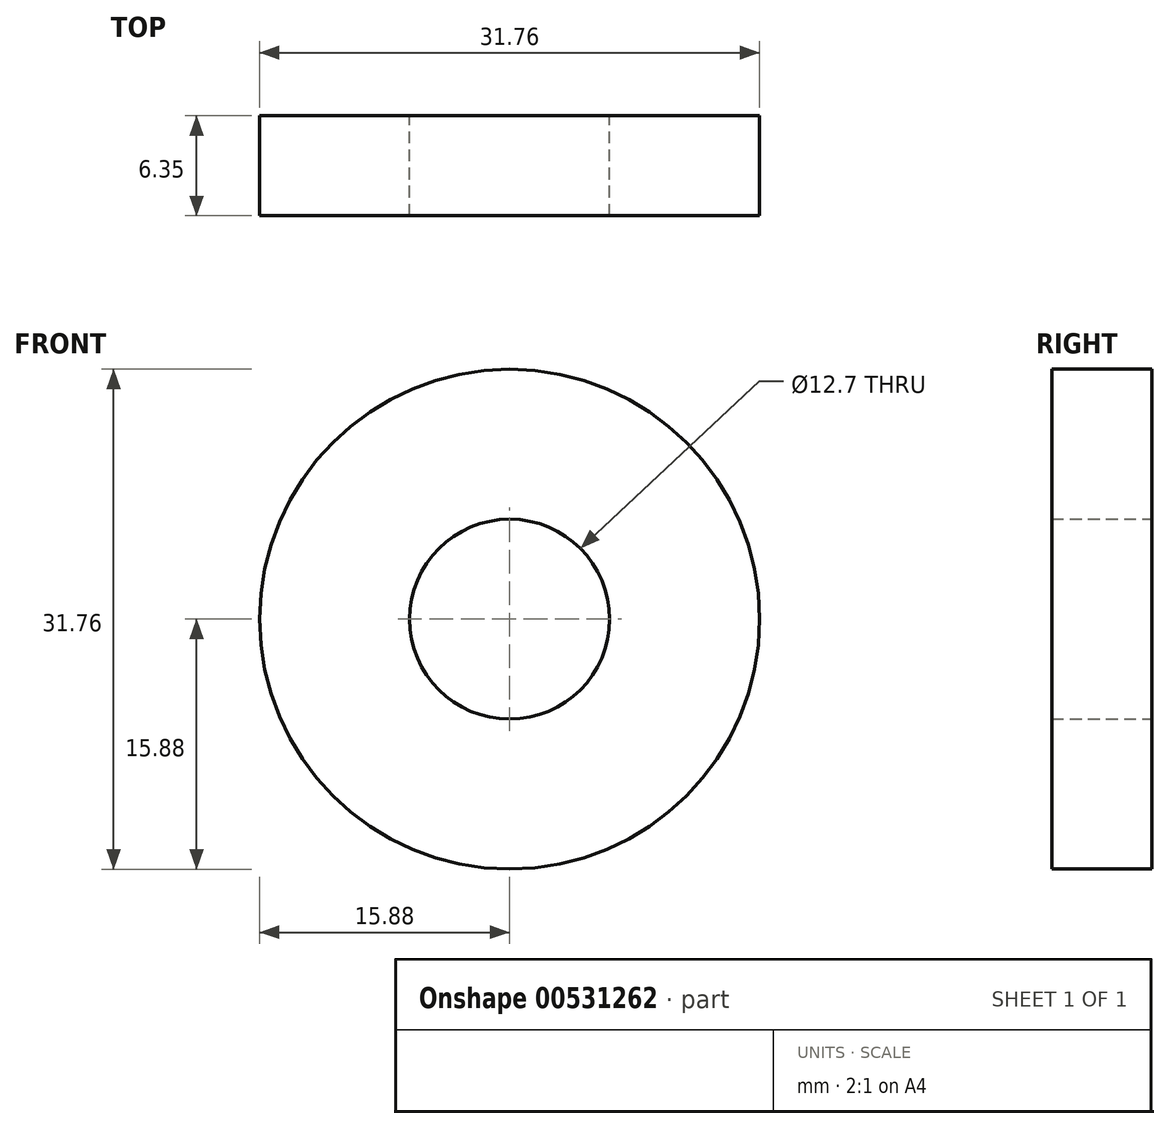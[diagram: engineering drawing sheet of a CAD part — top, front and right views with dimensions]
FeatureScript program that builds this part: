
annotation { "Feature Type Name" : "Feature", "Feature Type Description" : "" }
export const myFeature = defineFeature(function(context is Context, id is Id, definition is map)
    precondition{}
    {
        {
            var Q0;
            Q0=qCreatedBy(makeId("Front.planeOp"),FACE);
            var sketch = newSketch(context, id + "F0", { "sketchPlane" : qUnion([Q0])});
            skCircle(sketch, "E0", {"center": v(0, 0) * mm, "radius": 15.88 * mm});
            skCircle(sketch, "E1", {"center": v(0, 0) * mm, "radius": 6.35 * mm});
            skSolve(sketch);
        }
        {
            var Q0;
            Q0=makeQuery(id+"F0.imprint","IMPRINT",FACE,{"disambiguationData":[TD([[makeQuery(id+"F0.imprint","IMPRINT",EDGE,{"derivedFrom":sQuery(id+"F0.wireOp",EDGE,"E0")}),1.0]])]});
            extrude(context, id + "F1", {"entities" : qUnion([Q0]), "depth" : 6.35 * mm, "offsetDistance" : 25.4 * mm});
        }
    });
